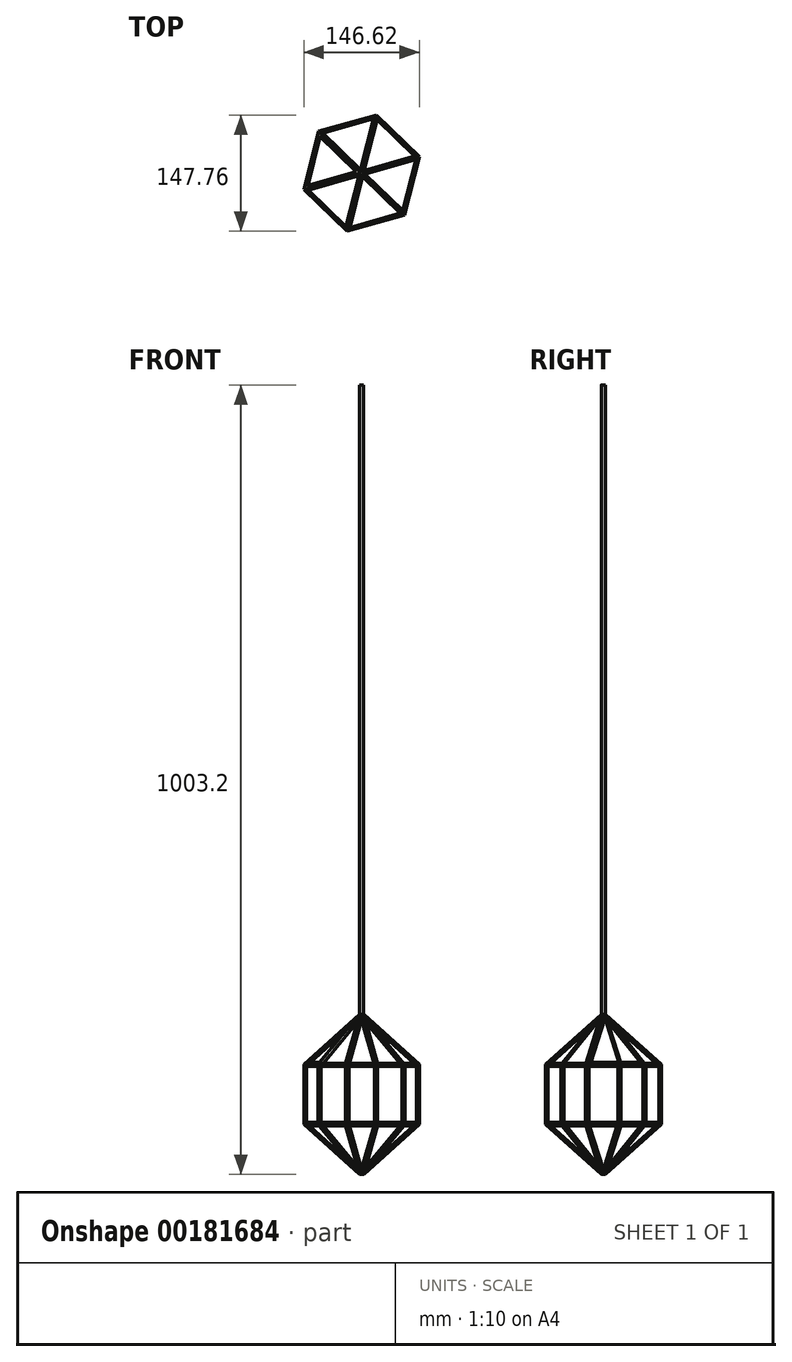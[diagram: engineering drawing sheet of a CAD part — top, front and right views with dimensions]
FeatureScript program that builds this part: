
annotation { "Feature Type Name" : "Feature", "Feature Type Description" : "" }
export const myFeature = defineFeature(function(context is Context, id is Id, definition is map)
    precondition{}
    {
        {
            var Q0;
            Q0=qCreatedBy(makeId("Top.planeOp"),FACE);
            var sketch = newSketch(context, id + "F0", { "sketchPlane" : qUnion([Q0])});
            skCircle(sketch, "E0.cCircle", {"center": v(0, 0) * mm, "radius": 66 * mm, "construction": true});
            skLineSegment(sketch, "E0.0", {"start": v(18.67, 73.88) * mm, "end": v(73.31, 20.77) * mm});
            skLineSegment(sketch, "E0.1", {"start": v(73.31, 20.77) * mm, "end": v(54.65, -53.1) * mm});
            skLineSegment(sketch, "E0.2", {"start": v(54.65, -53.1) * mm, "end": v(-18.67, -73.88) * mm});
            skLineSegment(sketch, "E0.3", {"start": v(-18.67, -73.88) * mm, "end": v(-73.31, -20.77) * mm});
            skLineSegment(sketch, "E0.4", {"start": v(-73.31, -20.77) * mm, "end": v(-54.65, 53.1) * mm});
            skLineSegment(sketch, "E0.5", {"start": v(-54.65, 53.1) * mm, "end": v(18.67, 73.88) * mm});
            skPoint(sketch, "E0.0.midPoint", {"position": v(45.99, 47.33) * mm});
            skSolve(sketch);
        }
        {
            var Q0;
            Q0=qSketchRegion(id+"F0",true);
            extrude(context, id + "F1", {"entities" : qUnion([Q0]), "depth" : 203.2 * mm});
        }
        {
            var Q0;
            Q0=makeQuery(id+"F1.opExtrude","CAP_FACE",FACE,{"disambiguationData":[OSD([sQuery(id+"F0.wireOp",EDGE,"E0.0"),sQuery(id+"F0.wireOp",EDGE,"E0.1"),sQuery(id+"F0.wireOp",EDGE,"E0.2"),sQuery(id+"F0.wireOp",EDGE,"E0.3"),sQuery(id+"F0.wireOp",EDGE,"E0.4"),sQuery(id+"F0.wireOp",EDGE,"E0.5")])],"isStart":false});
            var Q1;
            Q1=makeQuery(id+"F1.opExtrude","CAP_FACE",FACE,{"disambiguationData":[OSD([sQuery(id+"F0.wireOp",EDGE,"E0.0"),sQuery(id+"F0.wireOp",EDGE,"E0.1"),sQuery(id+"F0.wireOp",EDGE,"E0.2"),sQuery(id+"F0.wireOp",EDGE,"E0.3"),sQuery(id+"F0.wireOp",EDGE,"E0.4"),sQuery(id+"F0.wireOp",EDGE,"E0.5")])],"isStart":true});
            chamfer(context, id + "F2", {"entities" : qUnion([Q0, Q1]), "width" : 63.5 * mm, "tangentPropagation" : true});
        }
        {
            var Q0;
            {var subQ0=sQuery(id+"F0.wireOp",EDGE,"E0.4");Q0=makeQuery(id+"F2.opChamfer","BLEND_FACE",FACE,{"disambiguationData":[OSD([subQ0]),TDD([makeQuery(id+"F1.opExtrude","CAP_EDGE",EDGE,{"disambiguationData":[OSD([subQ0])],"isStart":false})])]});}
            var Q1;
            Q1=makeQuery(id+"F1.opExtrude","SWEPT_BODY",BODY,{"disambiguationData":[OSD([sQuery(id+"F0.wireOp",EDGE,"E0.0"),sQuery(id+"F0.wireOp",EDGE,"E0.1"),sQuery(id+"F0.wireOp",EDGE,"E0.2"),sQuery(id+"F0.wireOp",EDGE,"E0.3"),sQuery(id+"F0.wireOp",EDGE,"E0.4"),sQuery(id+"F0.wireOp",EDGE,"E0.5")])]});
            shell(context, id + "F3", {"entities" : qUnion([Q0]), "parts" : qUnion([Q1]), "thickness" : 2.54 * mm});
        }
        {
            var Q0;
            {var subQ0=sQuery(id+"F0.wireOp",EDGE,"E0.3");Q0=makeQuery(id+"F2.opChamfer","BLEND_FACE",FACE,{"disambiguationData":[OSD([subQ0]),TDD([makeQuery(id+"F1.opExtrude","CAP_EDGE",EDGE,{"disambiguationData":[OSD([subQ0])],"isStart":false})])]});}
            var sketch = newSketch(context, id + "F4", { "sketchPlane" : qUnion([Q0])});
            skLineSegment(sketch, "E1.0.0", {"start": v(60.92, 21.38) * mm, "end": v(81.56, 116.16) * mm});
            skLineSegment(sketch, "E1.0.1", {"start": v(81.56, 116.16) * mm, "end": v(79.19, 117.78) * mm});
            skLineSegment(sketch, "E1.0.2", {"start": v(-1.88, 64.53) * mm, "end": v(79.19, 117.78) * mm});
            skLineSegment(sketch, "E1.0.3", {"start": v(-1.88, 64.53) * mm, "end": v(60.92, 21.38) * mm});
            skLineSegment(sketch, "E2.0", {"start": v(59.24, 25.61) * mm, "end": v(78.56, 114.34) * mm});
            skLineSegment(sketch, "E2.1", {"start": v(2.67, 64.49) * mm, "end": v(59.24, 25.61) * mm});
            skLineSegment(sketch, "E2.2", {"start": v(2.67, 64.49) * mm, "end": v(78.56, 114.34) * mm});
            skSolve(sketch);
        }
        {
            var Q0;
            Q0=makeQuery(id+"F4.imprint","IMPRINT",FACE,{"disambiguationData":[TD([[makeQuery(id+"F4.imprint","IMPRINT",EDGE,{"derivedFrom":sQuery(id+"F4.wireOp",EDGE,"E2.0")}),1.0]])]});
            extrude(context, id + "F5", {"entities" : qUnion([Q0]), "operationType" : NewBodyOperationType.REMOVE, "endBound" : BoundingType.UP_TO_NEXT, "oppositeDirection" : true, "depth" : 25.4 * mm});
        }
        {
            var Q0;
            {var subQ0=sQuery(id+"F0.wireOp",EDGE,"E0.2");Q0=makeQuery(id+"F2.opChamfer","BLEND_FACE",FACE,{"disambiguationData":[OSD([subQ0]),TDD([makeQuery(id+"F1.opExtrude","CAP_EDGE",EDGE,{"disambiguationData":[OSD([subQ0])],"isStart":false})])]});}
            var sketch = newSketch(context, id + "F6", { "sketchPlane" : qUnion([Q0])});
            skLineSegment(sketch, "E3.0.0", {"start": v(27.12, 58.59) * mm, "end": v(-26.47, 139.44) * mm});
            skLineSegment(sketch, "E3.0.1", {"start": v(-26.47, 139.44) * mm, "end": v(-29.3, 138.87) * mm});
            skLineSegment(sketch, "E3.0.2", {"start": v(-47.6, 43.62) * mm, "end": v(-29.3, 138.87) * mm});
            skLineSegment(sketch, "E3.0.3", {"start": v(-47.6, 43.62) * mm, "end": v(27.12, 58.59) * mm});
            skLineSegment(sketch, "E4.0", {"start": v(22.91, 60.34) * mm, "end": v(-27.25, 136.02) * mm});
            skLineSegment(sketch, "E4.1", {"start": v(-44.39, 46.85) * mm, "end": v(22.91, 60.34) * mm});
            skLineSegment(sketch, "E4.2", {"start": v(-44.39, 46.85) * mm, "end": v(-27.25, 136.02) * mm});
            skSolve(sketch);
        }
        {
            var Q0;
            Q0=makeQuery(id+"F6.imprint","IMPRINT",FACE,{"disambiguationData":[TD([[makeQuery(id+"F6.imprint","IMPRINT",EDGE,{"derivedFrom":sQuery(id+"F6.wireOp",EDGE,"E4.0")}),1.0]])]});
            extrude(context, id + "F7", {"entities" : qUnion([Q0]), "operationType" : NewBodyOperationType.REMOVE, "endBound" : BoundingType.UP_TO_NEXT, "oppositeDirection" : true, "depth" : 25.4 * mm});
        }
        {
            var Q0;
            {var subQ0=sQuery(id+"F0.wireOp",EDGE,"E0.1");Q0=makeQuery(id+"F2.opChamfer","BLEND_FACE",FACE,{"disambiguationData":[OSD([subQ0]),TDD([makeQuery(id+"F1.opExtrude","CAP_EDGE",EDGE,{"disambiguationData":[OSD([subQ0])],"isStart":false})])]});}
            var sketch = newSketch(context, id + "F8", { "sketchPlane" : qUnion([Q0])});
            skLineSegment(sketch, "E5.0.0", {"start": v(-134.13, 46.4) * mm, "end": v(-61.9, -18.34) * mm});
            skLineSegment(sketch, "E5.0.1", {"start": v(-61.9, -18.34) * mm, "end": v(-36.26, 53.42) * mm});
            skLineSegment(sketch, "E5.0.2", {"start": v(-36.26, 53.42) * mm, "end": v(-133.16, 49.1) * mm});
            skLineSegment(sketch, "E5.0.3", {"start": v(-133.16, 49.1) * mm, "end": v(-134.13, 46.4) * mm});
            skLineSegment(sketch, "E6.0", {"start": v(-130.64, 46.68) * mm, "end": v(-63.02, -13.93) * mm});
            skLineSegment(sketch, "E6.1", {"start": v(-39.93, 50.71) * mm, "end": v(-130.64, 46.68) * mm});
            skLineSegment(sketch, "E6.2", {"start": v(-63.02, -13.93) * mm, "end": v(-39.93, 50.71) * mm});
            skSolve(sketch);
        }
        {
            var Q0;
            Q0=qSketchRegion(id+"F8",true);
            var Q1;
            {var subQ0=sQuery(id+"F8.wireOp",EDGE,"144117f5-ceeb-445f-adcc-b0d1e90e878f.3");Q1=makeQuery(id+"F8.imprint","IMPRINT",FACE,{"disambiguationData":[TD([[makeQuery(id+"F8.imprint","IMPRINT",EDGE,{"derivedFrom":subQ0}),1.0]])]});}
            extrude(context, id + "F9", {"entities" : qUnion([Q0, Q1]), "operationType" : NewBodyOperationType.REMOVE, "endBound" : BoundingType.UP_TO_NEXT, "oppositeDirection" : true, "depth" : 25.4 * mm});
        }
        {
            var Q0;
            Q0=qSketchRegion(id+"F8",true);
            var Q1;
            {var subQ0=sQuery(id+"F0.wireOp",EDGE,"E0.1");Q1=makeQuery(id+"F2.opChamfer","BLEND_FACE",FACE,{"disambiguationData":[OSD([subQ0]),TDD([makeQuery(id+"F1.opExtrude","CAP_EDGE",EDGE,{"disambiguationData":[OSD([subQ0])],"isStart":false})])]});}
            extrude(context, id + "F10", {"entities" : qUnion([Q0, Q1]), "operationType" : NewBodyOperationType.REMOVE, "endBound" : BoundingType.UP_TO_NEXT, "oppositeDirection" : true, "depth" : 25.4 * mm});
        }
        {
            var Q0;
            {var subQ0=sQuery(id+"F0.wireOp",EDGE,"E0.0");Q0=makeQuery(id+"F2.opChamfer","BLEND_FACE",FACE,{"disambiguationData":[OSD([subQ0]),TDD([makeQuery(id+"F1.opExtrude","CAP_EDGE",EDGE,{"disambiguationData":[OSD([subQ0])],"isStart":false})])]});}
            var sketch = newSketch(context, id + "F11", { "sketchPlane" : qUnion([Q0])});
            skLineSegment(sketch, "E7.0.0", {"start": v(-79.19, -117.78) * mm, "end": v(1.88, -64.53) * mm});
            skLineSegment(sketch, "E7.0.1", {"start": v(1.88, -64.53) * mm, "end": v(-60.92, -21.38) * mm});
            skLineSegment(sketch, "E7.0.2", {"start": v(-81.56, -116.16) * mm, "end": v(-60.92, -21.38) * mm});
            skLineSegment(sketch, "E7.0.3", {"start": v(-81.56, -116.16) * mm, "end": v(-79.19, -117.78) * mm});
            skLineSegment(sketch, "E8.0", {"start": v(-78.56, -114.34) * mm, "end": v(-59.24, -25.61) * mm});
            skLineSegment(sketch, "E8.1", {"start": v(-78.56, -114.34) * mm, "end": v(-2.67, -64.49) * mm});
            skLineSegment(sketch, "E8.2", {"start": v(-2.67, -64.49) * mm, "end": v(-59.24, -25.61) * mm});
            skSolve(sketch);
        }
        {
            var Q0;
            Q0=makeQuery(id+"F11.imprint","IMPRINT",FACE,{"disambiguationData":[TD([[makeQuery(id+"F11.imprint","IMPRINT",EDGE,{"derivedFrom":sQuery(id+"F11.wireOp",EDGE,"E8.0")}),-1.0]])]});
            extrude(context, id + "F12", {"entities" : qUnion([Q0]), "operationType" : NewBodyOperationType.REMOVE, "endBound" : BoundingType.UP_TO_NEXT, "oppositeDirection" : true, "depth" : 25.4 * mm});
        }
        {
            var Q0;
            {var subQ0=sQuery(id+"F0.wireOp",EDGE,"E0.5");Q0=makeQuery(id+"F2.opChamfer","BLEND_FACE",FACE,{"disambiguationData":[OSD([subQ0]),TDD([makeQuery(id+"F1.opExtrude","CAP_EDGE",EDGE,{"disambiguationData":[OSD([subQ0])],"isStart":false})])]});}
            var sketch = newSketch(context, id + "F13", { "sketchPlane" : qUnion([Q0])});
            skLineSegment(sketch, "E9.0.0", {"start": v(-27.12, -58.59) * mm, "end": v(26.47, -139.44) * mm});
            skLineSegment(sketch, "E9.0.1", {"start": v(26.47, -139.44) * mm, "end": v(29.3, -138.87) * mm});
            skLineSegment(sketch, "E9.0.2", {"start": v(29.3, -138.87) * mm, "end": v(47.6, -43.62) * mm});
            skLineSegment(sketch, "E9.0.3", {"start": v(47.6, -43.62) * mm, "end": v(-27.12, -58.59) * mm});
            skLineSegment(sketch, "E10.0", {"start": v(-22.91, -60.34) * mm, "end": v(27.25, -136.02) * mm});
            skLineSegment(sketch, "E10.1", {"start": v(44.39, -46.85) * mm, "end": v(-22.91, -60.34) * mm});
            skLineSegment(sketch, "E10.2", {"start": v(27.25, -136.02) * mm, "end": v(44.39, -46.85) * mm});
            skSolve(sketch);
        }
        {
            var Q0;
            Q0=makeQuery(id+"F13.imprint","IMPRINT",FACE,{"disambiguationData":[TD([[makeQuery(id+"F13.imprint","IMPRINT",EDGE,{"derivedFrom":sQuery(id+"F13.wireOp",EDGE,"E10.0")}),1.0]])]});
            extrude(context, id + "F14", {"entities" : qUnion([Q0]), "operationType" : NewBodyOperationType.REMOVE, "endBound" : BoundingType.UP_TO_NEXT, "oppositeDirection" : true, "depth" : 25.4 * mm});
        }
        {
            var Q0;
            Q0=makeQuery(id+"F1.opExtrude","SWEPT_FACE",FACE,{"disambiguationData":[OSD([sQuery(id+"F0.wireOp",EDGE,"E0.2")])]});
            var sketch = newSketch(context, id + "F15", { "sketchPlane" : qUnion([Q0])});
            skLineSegment(sketch, "E11.0.0", {"start": v(-38.1, 139.7) * mm, "end": v(-38.1, 63.5) * mm});
            skLineSegment(sketch, "E11.0.1", {"start": v(-38.1, 63.5) * mm, "end": v(38.1, 63.5) * mm});
            skLineSegment(sketch, "E11.0.2", {"start": v(38.1, 63.5) * mm, "end": v(38.1, 139.7) * mm});
            skLineSegment(sketch, "E11.0.3", {"start": v(38.1, 139.7) * mm, "end": v(-38.1, 139.7) * mm});
            skLineSegment(sketch, "E12.0", {"start": v(-35.56, 137.16) * mm, "end": v(-35.56, 66.04) * mm});
            skLineSegment(sketch, "E12.1", {"start": v(35.56, 137.16) * mm, "end": v(-35.56, 137.16) * mm});
            skLineSegment(sketch, "E12.2", {"start": v(35.56, 66.04) * mm, "end": v(35.56, 137.16) * mm});
            skLineSegment(sketch, "E12.3", {"start": v(-35.56, 66.04) * mm, "end": v(35.56, 66.04) * mm});
            skSolve(sketch);
        }
        {
            var Q0;
            Q0=makeQuery(id+"F15.imprint","IMPRINT",FACE,{"disambiguationData":[TD([[makeQuery(id+"F15.imprint","IMPRINT",EDGE,{"derivedFrom":sQuery(id+"F15.wireOp",EDGE,"E12.0")}),1.0]])]});
            extrude(context, id + "F16", {"entities" : qUnion([Q0]), "operationType" : NewBodyOperationType.REMOVE, "endBound" : BoundingType.THROUGH_ALL, "oppositeDirection" : true, "depth" : 25.4 * mm});
        }
        {
            var Q0;
            Q0=makeQuery(id+"F1.opExtrude","SWEPT_FACE",FACE,{"disambiguationData":[OSD([sQuery(id+"F0.wireOp",EDGE,"E0.1")])]});
            var sketch = newSketch(context, id + "F17", { "sketchPlane" : qUnion([Q0])});
            skLineSegment(sketch, "E13.0.0", {"start": v(-38.1, 139.7) * mm, "end": v(-38.1, 63.5) * mm});
            skLineSegment(sketch, "E13.0.1", {"start": v(-38.1, 63.5) * mm, "end": v(38.1, 63.5) * mm});
            skLineSegment(sketch, "E13.0.2", {"start": v(38.1, 63.5) * mm, "end": v(38.1, 139.7) * mm});
            skLineSegment(sketch, "E13.0.3", {"start": v(38.1, 139.7) * mm, "end": v(-38.1, 139.7) * mm});
            skLineSegment(sketch, "E14.0", {"start": v(35.56, 137.16) * mm, "end": v(-35.56, 137.16) * mm});
            skLineSegment(sketch, "E14.1", {"start": v(35.56, 66.04) * mm, "end": v(35.56, 137.16) * mm});
            skLineSegment(sketch, "E14.2", {"start": v(-35.56, 66.04) * mm, "end": v(35.56, 66.04) * mm});
            skLineSegment(sketch, "E14.3", {"start": v(-35.56, 137.16) * mm, "end": v(-35.56, 66.04) * mm});
            skSolve(sketch);
        }
        {
            var Q0;
            Q0=makeQuery(id+"F17.imprint","IMPRINT",FACE,{"disambiguationData":[TD([[makeQuery(id+"F17.imprint","IMPRINT",EDGE,{"derivedFrom":sQuery(id+"F17.wireOp",EDGE,"E14.0")}),1.0]])]});
            extrude(context, id + "F18", {"entities" : qUnion([Q0]), "operationType" : NewBodyOperationType.REMOVE, "endBound" : BoundingType.THROUGH_ALL, "oppositeDirection" : true, "depth" : 25.4 * mm});
        }
        {
            var Q0;
            Q0=makeQuery(id+"F1.opExtrude","SWEPT_FACE",FACE,{"disambiguationData":[OSD([sQuery(id+"F0.wireOp",EDGE,"E0.0")])]});
            var sketch = newSketch(context, id + "F19", { "sketchPlane" : qUnion([Q0])});
            skLineSegment(sketch, "E15.0.0", {"start": v(-38.1, 139.7) * mm, "end": v(-38.1, 63.5) * mm});
            skLineSegment(sketch, "E15.0.1", {"start": v(-38.1, 63.5) * mm, "end": v(38.1, 63.5) * mm});
            skLineSegment(sketch, "E15.0.2", {"start": v(38.1, 63.5) * mm, "end": v(38.1, 139.7) * mm});
            skLineSegment(sketch, "E15.0.3", {"start": v(38.1, 139.7) * mm, "end": v(-38.1, 139.7) * mm});
            skLineSegment(sketch, "E16.0", {"start": v(35.56, 137.16) * mm, "end": v(-35.56, 137.16) * mm});
            skLineSegment(sketch, "E16.1", {"start": v(35.56, 66.04) * mm, "end": v(35.56, 137.16) * mm});
            skLineSegment(sketch, "E16.2", {"start": v(-35.56, 66.04) * mm, "end": v(35.56, 66.04) * mm});
            skLineSegment(sketch, "E16.3", {"start": v(-35.56, 137.16) * mm, "end": v(-35.56, 66.04) * mm});
            skSolve(sketch);
        }
        {
            var Q0;
            Q0=makeQuery(id+"F19.imprint","IMPRINT",FACE,{"disambiguationData":[TD([[makeQuery(id+"F19.imprint","IMPRINT",EDGE,{"derivedFrom":sQuery(id+"F19.wireOp",EDGE,"E16.0")}),1.0]])]});
            extrude(context, id + "F20", {"entities" : qUnion([Q0]), "operationType" : NewBodyOperationType.REMOVE, "endBound" : BoundingType.THROUGH_ALL, "oppositeDirection" : true, "depth" : 25.4 * mm});
        }
        {
            var Q0;
            {var subQ0=sQuery(id+"F0.wireOp",EDGE,"E0.1");Q0=makeQuery(id+"F2.opChamfer","BLEND_FACE",FACE,{"disambiguationData":[OSD([subQ0]),TDD([makeQuery(id+"F1.opExtrude","CAP_EDGE",EDGE,{"disambiguationData":[OSD([subQ0])],"isStart":true})])]});}
            var sketch = newSketch(context, id + "F21", { "sketchPlane" : qUnion([Q0])});
            skLineSegment(sketch, "E17.0.0", {"start": v(73.4, 66.69) * mm, "end": v(1.17, 1.95) * mm});
            skLineSegment(sketch, "E17.0.1", {"start": v(1.17, 1.95) * mm, "end": v(2.14, -0.76) * mm});
            skLineSegment(sketch, "E17.0.2", {"start": v(2.14, -0.76) * mm, "end": v(99.04, -5.07) * mm});
            skLineSegment(sketch, "E17.0.3", {"start": v(99.04, -5.07) * mm, "end": v(73.4, 66.69) * mm});
            skLineSegment(sketch, "E18.0", {"start": v(72.29, 62.27) * mm, "end": v(4.67, 1.67) * mm});
            skLineSegment(sketch, "E18.1", {"start": v(95.38, -2.36) * mm, "end": v(72.29, 62.27) * mm});
            skLineSegment(sketch, "E18.2", {"start": v(4.67, 1.67) * mm, "end": v(95.38, -2.36) * mm});
            skLineSegment(sketch, "E19.0", {"start": v(76.2, 77.72) * mm, "end": v(-6.24, 3.83) * mm});
            skLineSegment(sketch, "E19.1", {"start": v(108.2, -11.83) * mm, "end": v(76.2, 77.72) * mm});
            skLineSegment(sketch, "E19.2", {"start": v(-2.4, -6.92) * mm, "end": v(108.2, -11.83) * mm});
            skLineSegment(sketch, "E19.3", {"start": v(-6.24, 3.83) * mm, "end": v(-2.4, -6.92) * mm});
            skSolve(sketch);
        }
        {
            var Q0;
            Q0=makeQuery(id+"F21.imprint","IMPRINT",FACE,{"disambiguationData":[TD([[makeQuery(id+"F21.imprint","IMPRINT",EDGE,{"derivedFrom":sQuery(id+"F21.wireOp",EDGE,"E18.0")}),1.0]])]});
            extrude(context, id + "F22", {"entities" : qUnion([Q0]), "operationType" : NewBodyOperationType.REMOVE, "endBound" : BoundingType.UP_TO_NEXT, "oppositeDirection" : true, "depth" : 25.4 * mm});
        }
        {
            var Q0;
            {var subQ0=sQuery(id+"F0.wireOp",EDGE,"E0.0");Q0=makeQuery(id+"F2.opChamfer","BLEND_FACE",FACE,{"disambiguationData":[OSD([subQ0]),TDD([makeQuery(id+"F1.opExtrude","CAP_EDGE",EDGE,{"disambiguationData":[OSD([subQ0])],"isStart":true})])]});}
            var sketch = newSketch(context, id + "F23", { "sketchPlane" : qUnion([Q0])});
            skLineSegment(sketch, "E20.0.0", {"start": v(83.26, -53.89) * mm, "end": v(2.18, -0.64) * mm});
            skLineSegment(sketch, "E20.0.1", {"start": v(2.18, -0.64) * mm, "end": v(-0.19, -2.27) * mm});
            skLineSegment(sketch, "E20.0.2", {"start": v(20.45, -97.04) * mm, "end": v(-0.19, -2.27) * mm});
            skLineSegment(sketch, "E20.0.3", {"start": v(20.45, -97.04) * mm, "end": v(83.26, -53.89) * mm});
            skLineSegment(sketch, "E21.0", {"start": v(78.7, -53.94) * mm, "end": v(2.8, -4.09) * mm});
            skLineSegment(sketch, "E21.1", {"start": v(22.13, -92.8) * mm, "end": v(78.7, -53.94) * mm});
            skLineSegment(sketch, "E21.2", {"start": v(22.13, -92.8) * mm, "end": v(2.8, -4.09) * mm});
            skSolve(sketch);
        }
        {
            var Q0;
            Q0=makeQuery(id+"F23.imprint","IMPRINT",FACE,{"disambiguationData":[TD([[makeQuery(id+"F23.imprint","IMPRINT",EDGE,{"derivedFrom":sQuery(id+"F23.wireOp",EDGE,"E21.0")}),1.0]])]});
            extrude(context, id + "F24", {"entities" : qUnion([Q0]), "operationType" : NewBodyOperationType.REMOVE, "endBound" : BoundingType.UP_TO_NEXT, "oppositeDirection" : true, "depth" : 25.4 * mm});
        }
        {
            var Q0;
            {var subQ0=sQuery(id+"F0.wireOp",EDGE,"E0.5");Q0=makeQuery(id+"F2.opChamfer","BLEND_FACE",FACE,{"disambiguationData":[OSD([subQ0]),TDD([makeQuery(id+"F1.opExtrude","CAP_EDGE",EDGE,{"disambiguationData":[OSD([subQ0])],"isStart":true})])]});}
            var sketch = newSketch(context, id + "F25", { "sketchPlane" : qUnion([Q0])});
            skLineSegment(sketch, "E22.0.0", {"start": v(-1.76, -1.44) * mm, "end": v(-55.35, -82.3) * mm});
            skLineSegment(sketch, "E22.0.1", {"start": v(-55.35, -82.3) * mm, "end": v(19.37, -97.26) * mm});
            skLineSegment(sketch, "E22.0.2", {"start": v(19.37, -97.26) * mm, "end": v(1.06, -2) * mm});
            skLineSegment(sketch, "E22.0.3", {"start": v(1.06, -2) * mm, "end": v(-1.76, -1.44) * mm});
            skLineSegment(sketch, "E23.0", {"start": v(-0.97, -4.86) * mm, "end": v(-51.14, -80.55) * mm});
            skLineSegment(sketch, "E23.1", {"start": v(16.16, -94.03) * mm, "end": v(-0.97, -4.86) * mm});
            skLineSegment(sketch, "E23.2", {"start": v(-51.14, -80.55) * mm, "end": v(16.16, -94.03) * mm});
            skLineSegment(sketch, "E24.0", {"start": v(-4.7, 5.62) * mm, "end": v(-65.86, -86.66) * mm});
            skLineSegment(sketch, "E24.1", {"start": v(6.5, 3.38) * mm, "end": v(-4.7, 5.62) * mm});
            skLineSegment(sketch, "E24.2", {"start": v(27.39, -105.35) * mm, "end": v(6.5, 3.38) * mm});
            skLineSegment(sketch, "E24.3", {"start": v(-65.86, -86.66) * mm, "end": v(27.39, -105.35) * mm});
            skSolve(sketch);
        }
        {
            var Q0;
            Q0=makeQuery(id+"F25.imprint","IMPRINT",FACE,{"disambiguationData":[TD([[makeQuery(id+"F25.imprint","IMPRINT",EDGE,{"derivedFrom":sQuery(id+"F25.wireOp",EDGE,"E23.0")}),1.0]])]});
            extrude(context, id + "F26", {"entities" : qUnion([Q0]), "operationType" : NewBodyOperationType.REMOVE, "endBound" : BoundingType.UP_TO_NEXT, "oppositeDirection" : true, "depth" : 25.4 * mm});
        }
        {
            var Q0;
            {var subQ0=sQuery(id+"F0.wireOp",EDGE,"E0.4");Q0=makeQuery(id+"F2.opChamfer","BLEND_FACE",FACE,{"disambiguationData":[OSD([subQ0]),TDD([makeQuery(id+"F1.opExtrude","CAP_EDGE",EDGE,{"disambiguationData":[OSD([subQ0])],"isStart":true})])]});}
            var sketch = newSketch(context, id + "F27", { "sketchPlane" : qUnion([Q0])});
            skLineSegment(sketch, "E25.0.0", {"start": v(-2.14, 0.76) * mm, "end": v(-99.04, 5.07) * mm});
            skLineSegment(sketch, "E25.0.1", {"start": v(-99.04, 5.07) * mm, "end": v(-73.4, -66.69) * mm});
            skLineSegment(sketch, "E25.0.2", {"start": v(-1.17, -1.95) * mm, "end": v(-73.4, -66.69) * mm});
            skLineSegment(sketch, "E25.0.3", {"start": v(-1.17, -1.95) * mm, "end": v(-2.14, 0.76) * mm});
            skLineSegment(sketch, "E26.0", {"start": v(-4.67, -1.67) * mm, "end": v(-95.38, 2.36) * mm});
            skLineSegment(sketch, "E26.1", {"start": v(-4.67, -1.67) * mm, "end": v(-72.29, -62.27) * mm});
            skLineSegment(sketch, "E26.2", {"start": v(-95.38, 2.36) * mm, "end": v(-72.29, -62.27) * mm});
            skSolve(sketch);
        }
        {
            var Q0;
            Q0=makeQuery(id+"F27.imprint","IMPRINT",FACE,{"disambiguationData":[TD([[makeQuery(id+"F27.imprint","IMPRINT",EDGE,{"derivedFrom":sQuery(id+"F27.wireOp",EDGE,"E26.0")}),1.0]])]});
            extrude(context, id + "F28", {"entities" : qUnion([Q0]), "operationType" : NewBodyOperationType.REMOVE, "endBound" : BoundingType.UP_TO_NEXT, "oppositeDirection" : true, "depth" : 25.4 * mm});
        }
        {
            var Q0;
            {var subQ0=sQuery(id+"F0.wireOp",EDGE,"E0.3");Q0=makeQuery(id+"F2.opChamfer","BLEND_FACE",FACE,{"disambiguationData":[OSD([subQ0]),TDD([makeQuery(id+"F1.opExtrude","CAP_EDGE",EDGE,{"disambiguationData":[OSD([subQ0])],"isStart":true})])]});}
            var sketch = newSketch(context, id + "F29", { "sketchPlane" : qUnion([Q0])});
            skLineSegment(sketch, "E27.0.0", {"start": v(0.19, 2.27) * mm, "end": v(-20.45, 97.04) * mm});
            skLineSegment(sketch, "E27.0.1", {"start": v(-20.45, 97.04) * mm, "end": v(-83.26, 53.89) * mm});
            skLineSegment(sketch, "E27.0.2", {"start": v(-2.18, 0.64) * mm, "end": v(-83.26, 53.89) * mm});
            skLineSegment(sketch, "E27.0.3", {"start": v(-2.18, 0.64) * mm, "end": v(0.19, 2.27) * mm});
            skLineSegment(sketch, "E28.0", {"start": v(-2.8, 4.09) * mm, "end": v(-22.13, 92.8) * mm});
            skLineSegment(sketch, "E28.1", {"start": v(-2.8, 4.09) * mm, "end": v(-78.7, 53.94) * mm});
            skLineSegment(sketch, "E28.2", {"start": v(-22.13, 92.8) * mm, "end": v(-78.7, 53.94) * mm});
            skSolve(sketch);
        }
        {
            var Q0;
            Q0=makeQuery(id+"F29.imprint","IMPRINT",FACE,{"disambiguationData":[TD([[makeQuery(id+"F29.imprint","IMPRINT",EDGE,{"derivedFrom":sQuery(id+"F29.wireOp",EDGE,"E28.0")}),1.0]])]});
            extrude(context, id + "F30", {"entities" : qUnion([Q0]), "operationType" : NewBodyOperationType.REMOVE, "endBound" : BoundingType.UP_TO_NEXT, "oppositeDirection" : true, "depth" : 25.4 * mm});
        }
        {
            var Q0;
            {var subQ0=sQuery(id+"F0.wireOp",EDGE,"E0.2");Q0=makeQuery(id+"F2.opChamfer","BLEND_FACE",FACE,{"disambiguationData":[OSD([subQ0]),TDD([makeQuery(id+"F1.opExtrude","CAP_EDGE",EDGE,{"disambiguationData":[OSD([subQ0])],"isStart":true})])]});}
            var sketch = newSketch(context, id + "F31", { "sketchPlane" : qUnion([Q0])});
            skLineSegment(sketch, "E29.0.0", {"start": v(1.76, 1.44) * mm, "end": v(55.35, 82.3) * mm});
            skLineSegment(sketch, "E29.0.1", {"start": v(55.35, 82.3) * mm, "end": v(-19.37, 97.26) * mm});
            skLineSegment(sketch, "E29.0.2", {"start": v(-1.06, 2) * mm, "end": v(-19.37, 97.26) * mm});
            skLineSegment(sketch, "E29.0.3", {"start": v(-1.06, 2) * mm, "end": v(1.76, 1.44) * mm});
            skLineSegment(sketch, "E30.0", {"start": v(0.97, 4.86) * mm, "end": v(51.14, 80.55) * mm});
            skLineSegment(sketch, "E30.1", {"start": v(0.97, 4.86) * mm, "end": v(-16.16, 94.03) * mm});
            skLineSegment(sketch, "E30.2", {"start": v(51.14, 80.55) * mm, "end": v(-16.16, 94.03) * mm});
            skSolve(sketch);
        }
        {
            var Q0;
            Q0=makeQuery(id+"F31.imprint","IMPRINT",FACE,{"disambiguationData":[TD([[makeQuery(id+"F31.imprint","IMPRINT",EDGE,{"derivedFrom":sQuery(id+"F31.wireOp",EDGE,"E30.0")}),1.0]])]});
            extrude(context, id + "F32", {"entities" : qUnion([Q0]), "operationType" : NewBodyOperationType.REMOVE, "endBound" : BoundingType.UP_TO_NEXT, "oppositeDirection" : true, "depth" : 25.4 * mm});
        }
        {
            var Q0;
            Q0=makeQuery(id+"F1.opExtrude","CAP_FACE",FACE,{"disambiguationData":[OSD([sQuery(id+"F0.wireOp",EDGE,"E0.0"),sQuery(id+"F0.wireOp",EDGE,"E0.1"),sQuery(id+"F0.wireOp",EDGE,"E0.2"),sQuery(id+"F0.wireOp",EDGE,"E0.3"),sQuery(id+"F0.wireOp",EDGE,"E0.4"),sQuery(id+"F0.wireOp",EDGE,"E0.5")])],"isStart":false});
            var sketch = newSketch(context, id + "F33", { "sketchPlane" : qUnion([Q0])});
            skCircle(sketch, "E31", {"center": v(0, 0) * mm, "radius": 2.54 * mm});
            skSolve(sketch);
        }
        {
            var Q0;
            Q0 = qSketchRegion(id + "F33", true);
            extrude(context, id + "F34", {"entities" : qUnion([Q0]), "operationType" : NewBodyOperationType.ADD, "depth" : 800 * mm});
        }
    });
